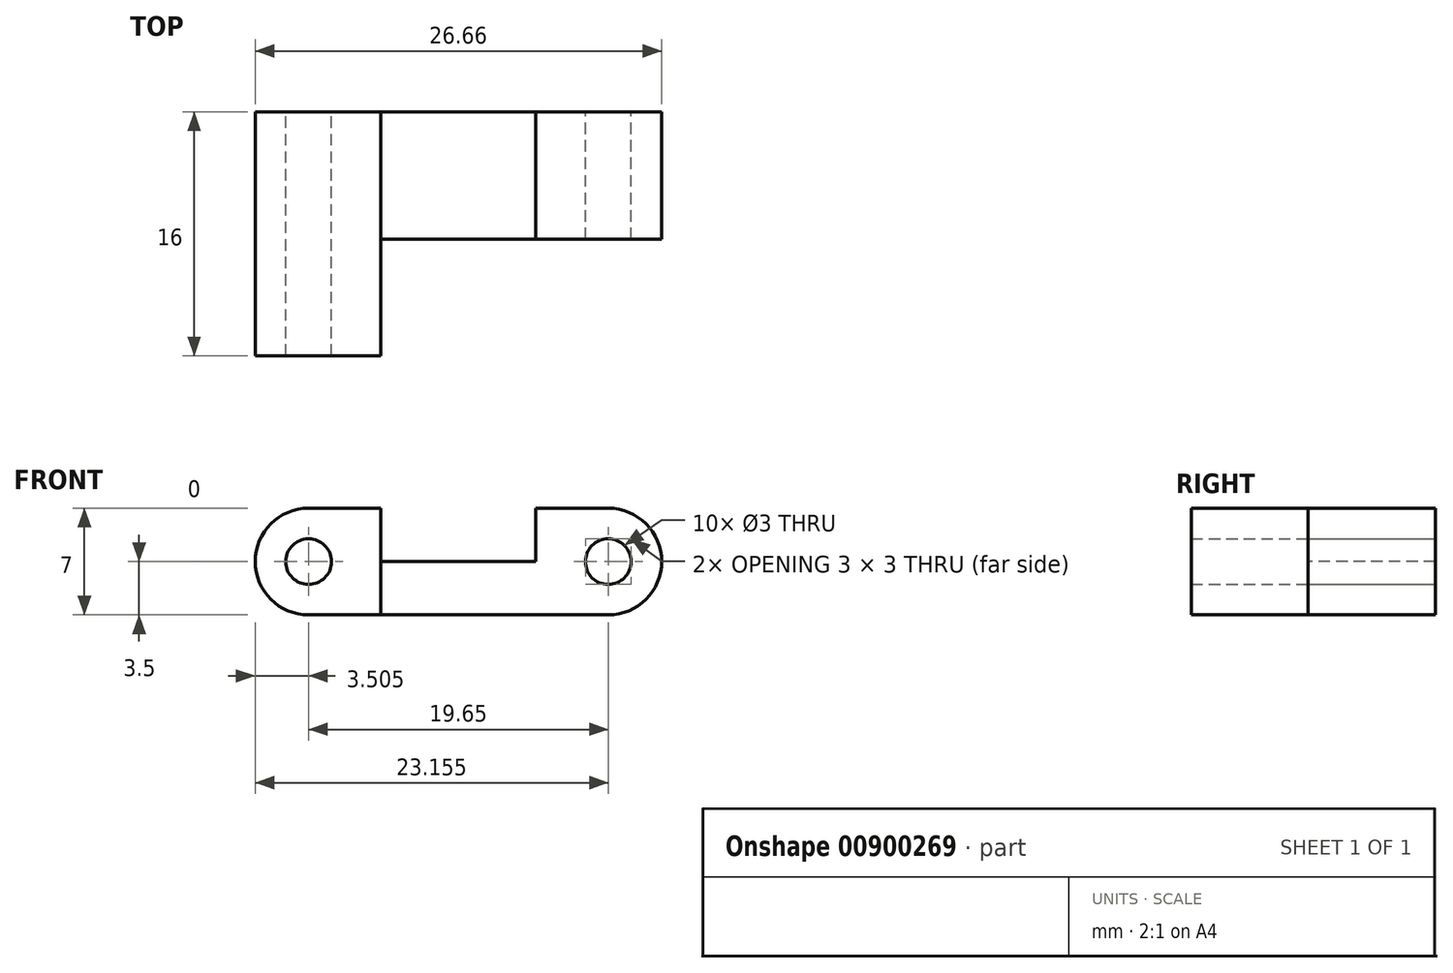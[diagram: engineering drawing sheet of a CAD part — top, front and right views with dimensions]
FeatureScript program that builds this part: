
annotation { "Feature Type Name" : "Feature", "Feature Type Description" : "" }
export const myFeature = defineFeature(function(context is Context, id is Id, definition is map)
    precondition{}
    {
        {
            var Q0;
            Q0=qCreatedBy(makeId("Front.planeOp"),FACE);
            var sketch = newSketch(context, id + "F0", { "sketchPlane" : qUnion([Q0])});
            skArc(sketch, "E0", {"start": v(-9.82, 3.5) * mm, "mid": v(-13.32, 0) * mm, "end": v(-9.82, -3.5) * mm});
            skArc(sketch, "E1", {"start": v(9.82, -3.5) * mm, "mid": v(13.32, 0) * mm, "end": v(9.83, 3.5) * mm});
            skLineSegment(sketch, "E2", {"start": v(-9.82, 3.5) * mm, "end": v(9.83, 3.5) * mm});
            skLineSegment(sketch, "E3", {"start": v(9.83, -3.5) * mm, "end": v(-9.82, -3.5) * mm});
            skCircle(sketch, "E4", {"center": v(9.83, 0) * mm, "radius": 1.5 * mm});
            skCircle(sketch, "E5", {"center": v(-9.82, 0) * mm, "radius": 1.5 * mm});
            skSolve(sketch);
        }
        {
            var Q0;
            Q0 = qSketchRegion(id + "F0", true);
            extrude(context, id + "F1", {"entities" : qUnion([Q0]), "endBound" : BoundingType.SYMMETRIC, "depth" : 16 * mm, "offsetDistance" : 25.4 * mm});
        }
        {
            var Q0;
            Q0=makeQuery(id+"F1.opExtrude","SWEPT_FACE",FACE,{"disambiguationData":[OSD([sQuery(id+"F0.wireOp",EDGE,"E2")])]});
            var sketch = newSketch(context, id + "F2", { "sketchPlane" : qUnion([Q0])});
            skLineSegment(sketch, "E6.bottom", {"start": v(25.15, -14.92) * mm, "end": v(-5.08, -14.92) * mm});
            skLineSegment(sketch, "E6.top", {"start": v(25.15, -0.35) * mm, "end": v(-5.08, -0.35) * mm});
            skLineSegment(sketch, "E6.left", {"start": v(25.15, -14.92) * mm, "end": v(25.15, -0.35) * mm});
            skLineSegment(sketch, "E6.right", {"start": v(-5.08, -14.92) * mm, "end": v(-5.08, -0.35) * mm});
            skSolve(sketch);
        }
        {
            var Q0;
            Q0 = qSketchRegion(id + "F2", true);
            extrude(context, id + "F3", {"entities" : qUnion([Q0]), "operationType" : NewBodyOperationType.REMOVE, "oppositeDirection" : true, "depth" : 25.4 * mm, "offsetDistance" : 25.4 * mm});
        }
        {
            var Q0;
            Q0=makeQuery(id+"F3.boolean.opBoolean","COPY",FACE,{"derivedFrom":makeQuery(id+"F3.opExtrude","SWEPT_FACE",FACE,{"disambiguationData":[OSD([sQuery(id+"F2.wireOp",EDGE,"E6.top")])]})});
            var sketch = newSketch(context, id + "F4", { "sketchPlane" : qUnion([Q0])});
            skLineSegment(sketch, "E7.bottom", {"start": v(-5.08, 6.53) * mm, "end": v(5.08, 6.53) * mm});
            skLineSegment(sketch, "E7.top", {"start": v(-5.08, 0) * mm, "end": v(5.08, 0) * mm});
            skLineSegment(sketch, "E7.left", {"start": v(-5.08, 6.53) * mm, "end": v(-5.08, 0) * mm});
            skLineSegment(sketch, "E7.right", {"start": v(5.08, 6.53) * mm, "end": v(5.08, 0) * mm});
            skSolve(sketch);
        }
        {
            var Q0;
            Q0 = qSketchRegion(id + "F4", true);
            extrude(context, id + "F5", {"entities" : qUnion([Q0]), "operationType" : NewBodyOperationType.REMOVE, "oppositeDirection" : true, "depth" : 25.4 * mm, "offsetDistance" : 25.4 * mm});
        }
    });
